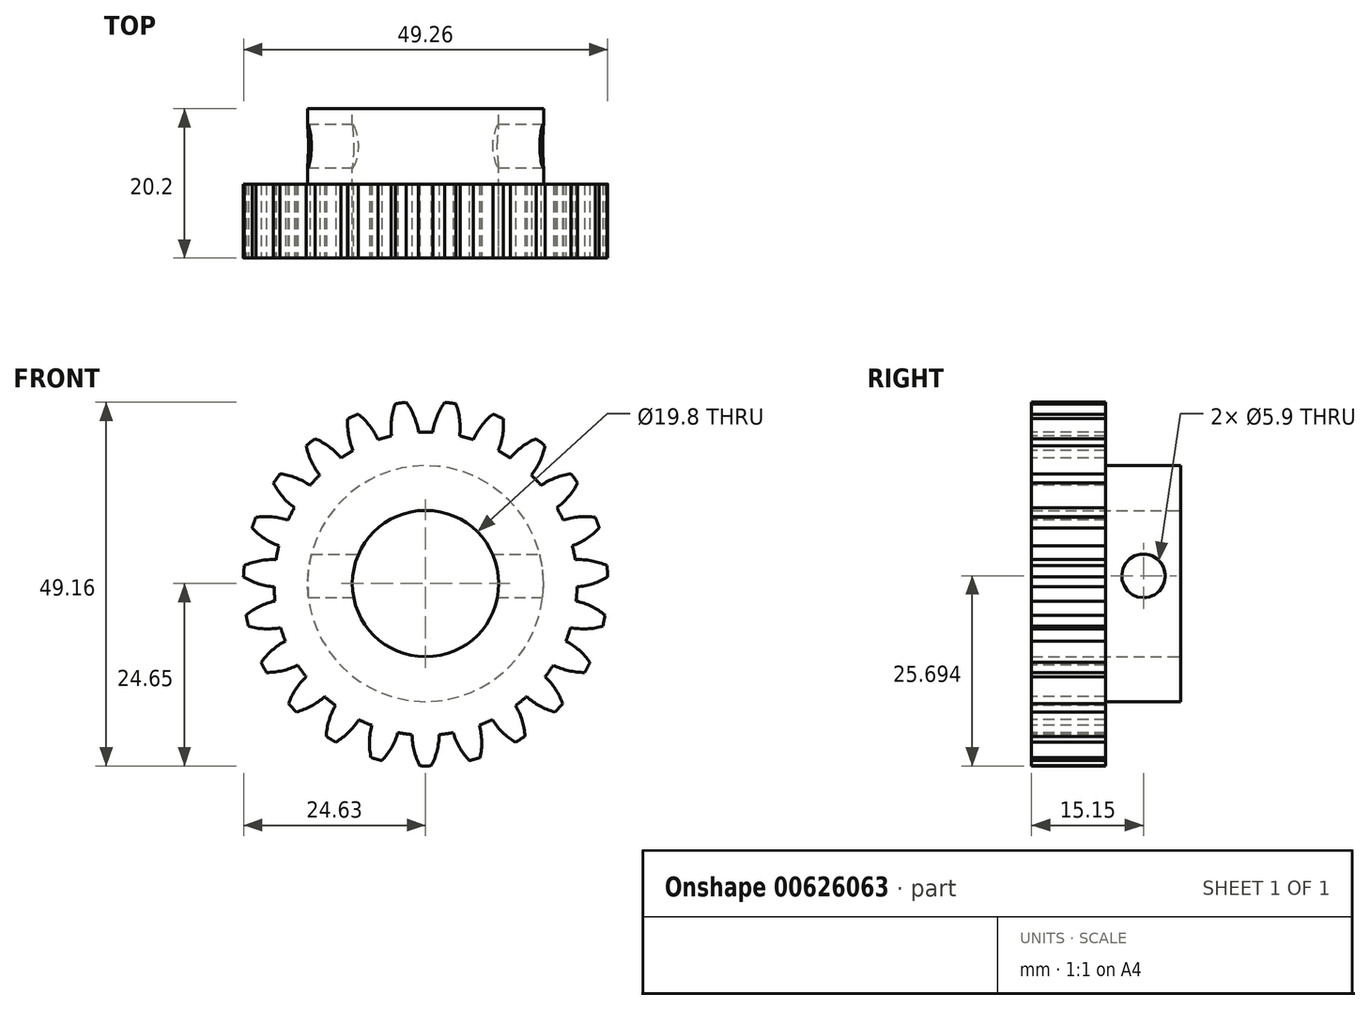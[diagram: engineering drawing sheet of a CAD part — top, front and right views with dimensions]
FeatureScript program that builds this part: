
annotation { "Feature Type Name" : "Feature", "Feature Type Description" : "" }
export const myFeature = defineFeature(function(context is Context, id is Id, definition is map)
    precondition{}
    {
        {
            var Q0;
            Q0=qCreatedBy(makeId("Right.planeOp"),FACE);
            var sketch = newSketch(context, id + "F0", { "sketchPlane" : qUnion([Q0])});
            skLineSegment(sketch, "E0", {"start": v(0, 0) * mm, "end": v(20.2, 0) * mm});
            skLineSegment(sketch, "E1", {"start": v(20.2, 0) * mm, "end": v(20.2, 15.95) * mm});
            skLineSegment(sketch, "E2", {"start": v(20.2, 15.95) * mm, "end": v(10, 15.95) * mm});
            skLineSegment(sketch, "E3", {"start": v(10, 15.95) * mm, "end": v(10, 24.65) * mm});
            skLineSegment(sketch, "E4", {"start": v(10, 24.65) * mm, "end": v(0, 24.65) * mm});
            skLineSegment(sketch, "E5", {"start": v(0, 24.65) * mm, "end": v(0, 0) * mm});
            skSolve(sketch);
        }
        {
            var Q0;
            Q0=makeQuery(id+"F0.imprint","IMPRINT",FACE,{"disambiguationData":[TD([[makeQuery(id+"F0.imprint","IMPRINT",EDGE,{"derivedFrom":sQuery(id+"F0.wireOp",EDGE,"E0")}),1.0]])]});
            var Q1;
            Q1=sQuery(id+"F0.wireOp",EDGE,"E0");
            revolve(context, id + "F1", {"entities" : qUnion([Q0]), "axis" : qUnion([Q1]), "revolveType" : RevolveType.FULL, "surfaceOperationType" : NewSurfaceOperationType.NEW});
        }
        {
            var Q0;
            Q0=makeQuery(id+"F1.opRevolve","SWEPT_FACE",FACE,{"disambiguationData":[OSD([sQuery(id+"F0.wireOp",EDGE,"E1")])]});
            var sketch = newSketch(context, id + "F2", { "sketchPlane" : qUnion([Q0])});
            skCircle(sketch, "E6", {"center": v(0, 0) * mm, "radius": 9.9 * mm});
            skSolve(sketch);
        }
        {
            var Q0;
            Q0=makeQuery(id+"F2.imprint","IMPRINT",FACE,{"disambiguationData":[TD([[makeQuery(id+"F2.imprint","IMPRINT",EDGE,{"derivedFrom":sQuery(id+"F2.wireOp",EDGE,"E6")}),1.0]])]});
            extrude(context, id + "F3", {"entities" : qUnion([Q0]), "operationType" : NewBodyOperationType.REMOVE, "oppositeDirection" : true, "depth" : 25 * mm, "offsetDistance" : 25 * mm});
        }
        {
            var Q0;
            Q0=makeQuery(id+"F1.opRevolve","SWEPT_FACE",FACE,{"disambiguationData":[OSD([sQuery(id+"F0.wireOp",EDGE,"E5")])]});
            var sketch = newSketch(context, id + "F4", { "sketchPlane" : qUnion([Q0])});
            skCircle(sketch, "E7", {"center": v(0, 0) * mm, "radius": 25.25 * mm});
            skCircle(sketch, "E8", {"center": v(0, 0) * mm, "radius": 21.61 * mm, "construction": true});
            skCircle(sketch, "E9", {"center": v(0, 0) * mm, "radius": 23 * mm, "construction": true});
            skCircle(sketch, "E10", {"center": v(0, 0) * mm, "radius": 20.5 * mm});
            skLineSegment(sketch, "E11", {"start": v(0, 0) * mm, "end": v(0, 40.59) * mm, "construction": true});
            skLineSegment(sketch, "E12", {"start": v(0, 0) * mm, "end": v(-5.97, 43.45) * mm, "construction": true});
            skLineSegment(sketch, "E13", {"start": v(-1.69, 22.94) * mm, "end": v(-4.58, 43.99) * mm, "construction": true});
            skArc(sketch, "E14", {"start": v(-0.96, 20.48) * mm, "mid": v(-1.68, 22.92) * mm, "end": v(-3.04, 25.07) * mm});
            skArc(sketch, "E15.MirrorCS", {"start": v(0.96, 20.48) * mm, "mid": v(1.68, 22.92) * mm, "end": v(3.04, 25.07) * mm});
            skSolve(sketch);
        }
        {
            var Q0;
            {var subQ0=sQuery(id+"F4.wireOp",EDGE,"E14");var subQ1=sQuery(id+"F4.wireOp",EDGE,"E10");var subQ2=makeQuery(id+"F4.imprint","INTERSECT",VERTEX,{"derivedFrom":[subQ1,subQ0]});Q0=makeQuery(id+"F4.imprint","IMPRINT",FACE,{"disambiguationData":[TD([[makeQuery(id+"F4.imprint","IMPRINT",EDGE,{"disambiguationData":[TD([[subQ2,1.0]])],"derivedFrom":subQ1}),-1.0]])]});}
            var Q1;
            {var subQ0=sQuery(id+"F4.wireOp",EDGE,"E14");var subQ1=sQuery(id+"F4.wireOp",EDGE,"E7");var subQ2=makeQuery(id+"F4.imprint","INTERSECT",VERTEX,{"derivedFrom":[subQ1,subQ0]});Q1=makeQuery(id+"F4.imprint","IMPRINT",FACE,{"disambiguationData":[TD([[makeQuery(id+"F4.imprint","IMPRINT",EDGE,{"disambiguationData":[TD([[subQ2,1.0]])],"derivedFrom":subQ1}),1.0]])]});}
            extrude(context, id + "F5", {"entities" : qUnion([Q0, Q1]), "operationType" : NewBodyOperationType.REMOVE, "oppositeDirection" : true, "depth" : 25 * mm, "offsetDistance" : 25 * mm});
        }
        {
            var Q0;
            Q0=makeQuery(id+"F5.boolean.opBoolean","COPY",FACE,{"derivedFrom":makeQuery(id+"F5.opExtrude","SWEPT_FACE",FACE,{"disambiguationData":[OSD([sQuery(id+"F4.wireOp",EDGE,"E14")])]})});
            var Q1;
            Q1=makeQuery(id+"F5.boolean.opBoolean","COPY",FACE,{"derivedFrom":makeQuery(id+"F5.opExtrude","SWEPT_FACE",FACE,{"disambiguationData":[OSD([sQuery(id+"F4.wireOp",EDGE,"E10")])]})});
            var Q2;
            Q2=makeQuery(id+"F5.boolean.opBoolean","COPY",FACE,{"derivedFrom":makeQuery(id+"F5.opExtrude","SWEPT_FACE",FACE,{"disambiguationData":[OSD([sQuery(id+"F4.wireOp",EDGE,"E15.MirrorCS")])]})});
            var Q3;
            Q3=makeQuery(id+"F1.opRevolve","SWEPT_FACE",FACE,{"disambiguationData":[OSD([sQuery(id+"F0.wireOp",EDGE,"E4")])]});
            circularPattern(context, id + "F6", {"patternType" : PatternType.FACE, "faces" : qUnion([Q0, Q1, Q2]), "axis" : qUnion([Q3]), "angle" : 360 * degree, "instanceCount" : 23, "equalSpace" : true});
        }
        {
            var Q0;
            Q0=qCreatedBy(makeId("Right.planeOp"),FACE);
            var sketch = newSketch(context, id + "F7", { "sketchPlane" : qUnion([Q0])});
            skCircle(sketch, "E16", {"center": v(15.15, 1.04) * mm, "radius": 2.95 * mm});
            skSolve(sketch);
        }
        {
            var Q0;
            Q0 = qSketchRegion(id + "F7", true);
            extrude(context, id + "F8", {"entities" : qUnion([Q0]), "operationType" : NewBodyOperationType.REMOVE, "oppositeDirection" : true, "depth" : 74.6 * mm, "offsetDistance" : 25 * mm, "symmetric" : true});
        }
    });
